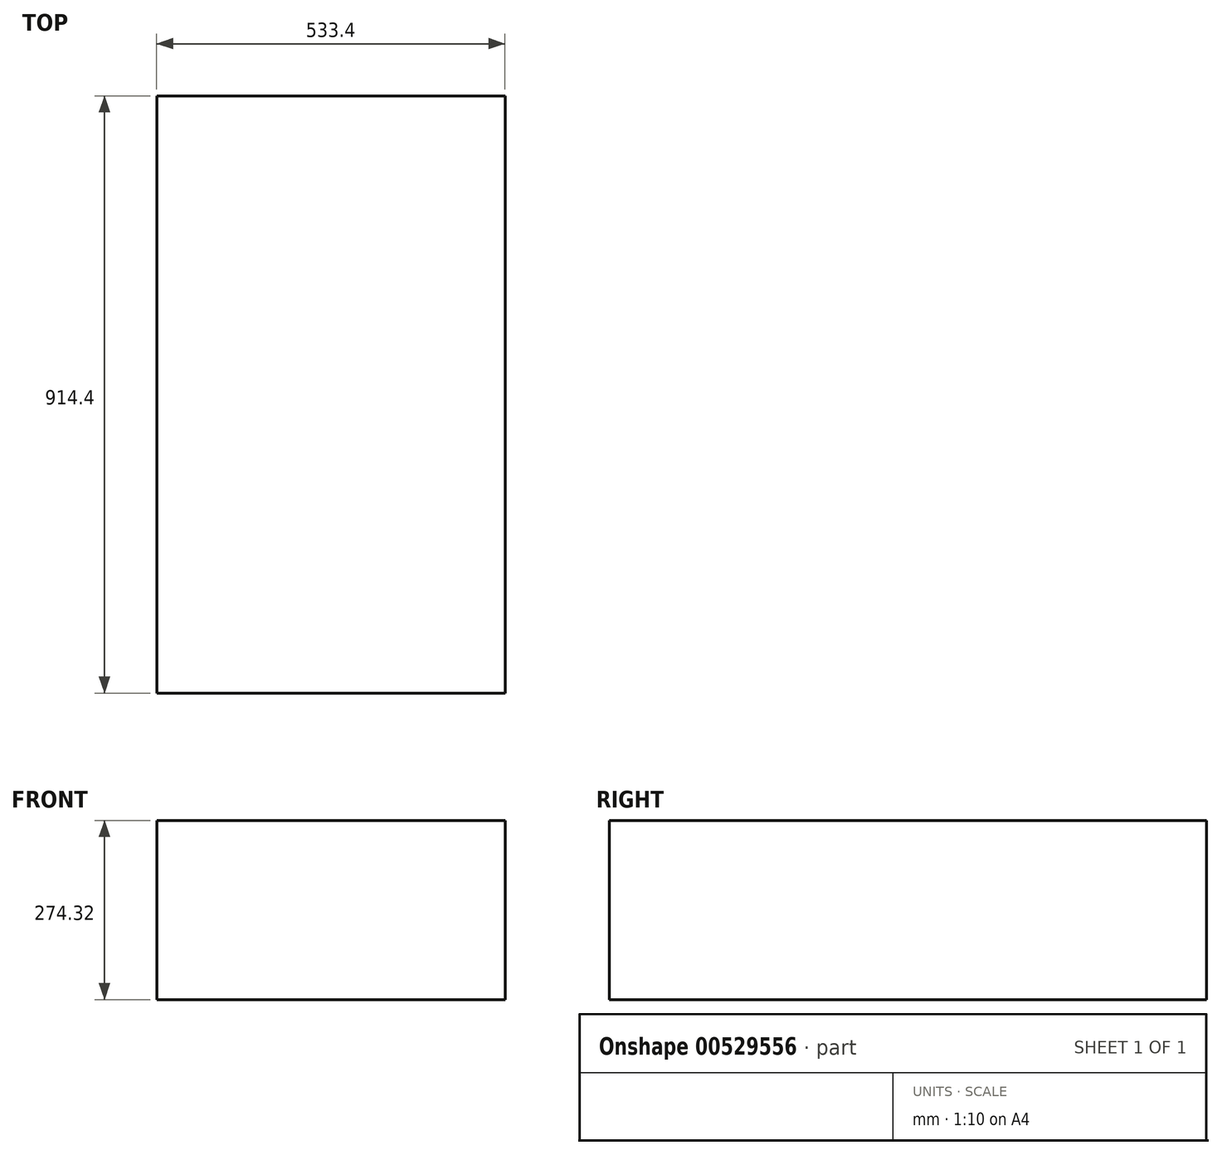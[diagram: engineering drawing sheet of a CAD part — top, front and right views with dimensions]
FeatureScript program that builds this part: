
annotation { "Feature Type Name" : "Feature", "Feature Type Description" : "" }
export const myFeature = defineFeature(function(context is Context, id is Id, definition is map)
    precondition{}
    {
        {
            var Q0;
            Q0=qCreatedBy(makeId("Top.planeOp"),FACE);
            var sketch = newSketch(context, id + "F0", { "sketchPlane" : qUnion([Q0])});
            skLineSegment(sketch, "E0.bottom", {"start": v(-266.03, 421.26) * mm, "end": v(267.37, 421.26) * mm});
            skLineSegment(sketch, "E0.top", {"start": v(-266.03, -493.14) * mm, "end": v(267.37, -493.14) * mm});
            skLineSegment(sketch, "E0.left", {"start": v(-266.03, 421.26) * mm, "end": v(-266.03, -493.14) * mm});
            skLineSegment(sketch, "E0.right", {"start": v(267.37, 421.26) * mm, "end": v(267.37, -493.14) * mm});
            skSolve(sketch);
        }
        {
            var Q0;
            Q0=makeQuery(id+"F0.imprint","IMPRINT",FACE,{"disambiguationData":[TD([[makeQuery(id+"F0.imprint","IMPRINT",EDGE,{"derivedFrom":sQuery(id+"F0.wireOp",EDGE,"E0.bottom")}),-1.0]])]});
            extrude(context, id + "F1", {"entities" : qUnion([Q0]), "depth" : 274.32 * mm, "offsetDistance" : 30.48 * mm});
        }
    });
